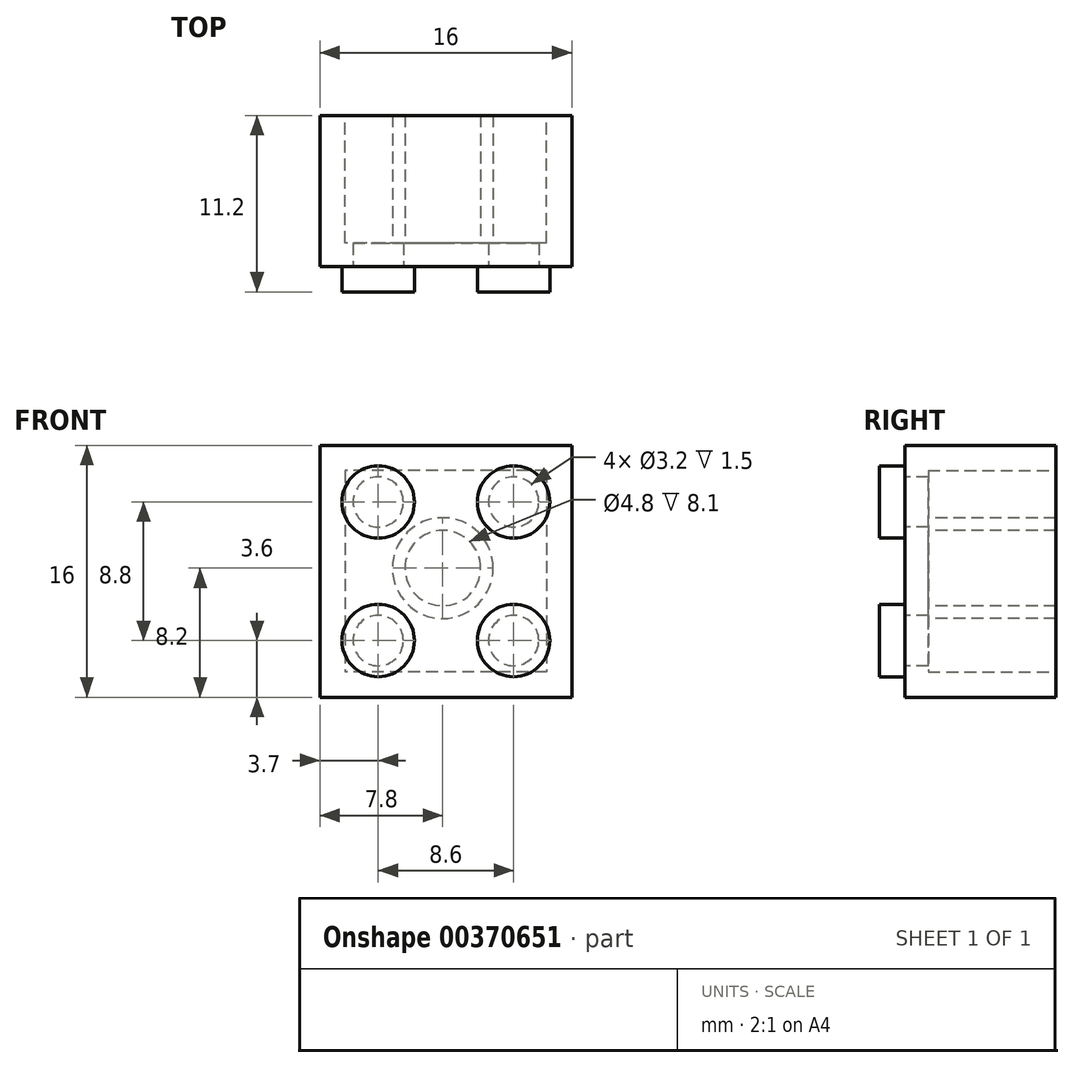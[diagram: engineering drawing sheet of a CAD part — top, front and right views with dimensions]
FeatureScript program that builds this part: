
annotation { "Feature Type Name" : "Feature", "Feature Type Description" : "" }
export const myFeature = defineFeature(function(context is Context, id is Id, definition is map)
    precondition{}
    {
        {
            var Q0;
            Q0=qCreatedBy(makeId("Front.planeOp"),FACE);
            var sketch = newSketch(context, id + "F0", { "sketchPlane" : qUnion([Q0])});
            skLineSegment(sketch, "E0.bottom", {"start": v(8, 8) * mm, "end": v(-8, 8) * mm});
            skLineSegment(sketch, "E0.top", {"start": v(8, -8) * mm, "end": v(-8, -8) * mm});
            skLineSegment(sketch, "E0.left", {"start": v(8, 8) * mm, "end": v(8, -8) * mm});
            skLineSegment(sketch, "E0.right", {"start": v(-8, 8) * mm, "end": v(-8, -8) * mm});
            skPoint(sketch, "E0.middle", {"position": v(0, 0) * mm});
            skLineSegment(sketch, "E1.0", {"start": v(6.4, 6.4) * mm, "end": v(-6.4, 6.4) * mm});
            skLineSegment(sketch, "E1.1", {"start": v(6.4, 6.4) * mm, "end": v(6.4, -6.4) * mm});
            skLineSegment(sketch, "E1.2", {"start": v(6.4, -6.4) * mm, "end": v(-6.4, -6.4) * mm});
            skLineSegment(sketch, "E1.3", {"start": v(-6.4, 6.4) * mm, "end": v(-6.4, -6.4) * mm});
            skSolve(sketch);
        }
        {
            var Q0;
            Q0 = qSketchRegion(id + "F0", true);
            var Q1;
            Q1=makeQuery(id+"F0.imprint","IMPRINT",FACE,{"disambiguationData":[TD([[makeQuery(id+"F0.imprint","IMPRINT",EDGE,{"derivedFrom":sQuery(id+"F0.wireOp",EDGE,"E1.0")}),1.0]])]});
            extrude(context, id + "F1", {"entities" : qUnion([Q0, Q1]), "depth" : 9.6 * mm});
        }
        {
            var Q0;
            Q0=makeQuery(id+"F0.imprint","IMPRINT",FACE,{"disambiguationData":[TD([[makeQuery(id+"F0.imprint","IMPRINT",EDGE,{"derivedFrom":sQuery(id+"F0.wireOp",EDGE,"E1.0")}),1.0]])]});
            extrude(context, id + "F2", {"entities" : qUnion([Q0]), "operationType" : NewBodyOperationType.REMOVE, "depth" : 8.1 * mm});
        }
        {
            var Q0;
            Q0=makeQuery(id+"F1.opExtrude","CAP_FACE",FACE,{"disambiguationData":[OSD([sQuery(id+"F0.wireOp",EDGE,"E0.bottom"),sQuery(id+"F0.wireOp",EDGE,"E0.top"),sQuery(id+"F0.wireOp",EDGE,"E0.left"),sQuery(id+"F0.wireOp",EDGE,"E0.right")])],"isStart":false});
            var sketch = newSketch(context, id + "F3", { "sketchPlane" : qUnion([Q0])});
            skCircle(sketch, "E2", {"center": v(-4.3, 4.4) * mm, "radius": 1.6 * mm});
            skCircle(sketch, "E3", {"center": v(-4.3, -4.4) * mm, "radius": 1.6 * mm});
            skCircle(sketch, "E4.MirrorC", {"center": v(4.3, 4.4) * mm, "radius": 1.6 * mm});
            skCircle(sketch, "E5.MirrorC", {"center": v(4.3, -4.4) * mm, "radius": 1.6 * mm});
            skSolve(sketch);
        }
        {
            var Q0;
            Q0 = qSketchRegion(id + "F3", true);
            extrude(context, id + "F4", {"entities" : qUnion([Q0]), "operationType" : NewBodyOperationType.REMOVE, "oppositeDirection" : true, "depth" : 1.6 * mm});
        }
        {
            var Q0;
            Q0=makeQuery(id+"F1.opExtrude","CAP_FACE",FACE,{"disambiguationData":[OSD([sQuery(id+"F0.wireOp",EDGE,"E0.bottom"),sQuery(id+"F0.wireOp",EDGE,"E0.top"),sQuery(id+"F0.wireOp",EDGE,"E0.left"),sQuery(id+"F0.wireOp",EDGE,"E0.right")])],"isStart":false});
            var sketch = newSketch(context, id + "F5", { "sketchPlane" : qUnion([Q0])});
            skCircle(sketch, "E6", {"center": v(-4.3, 4.4) * mm, "radius": 2.3 * mm});
            skCircle(sketch, "E7", {"center": v(-4.3, -4.4) * mm, "radius": 2.3 * mm});
            skCircle(sketch, "E8.MirrorC", {"center": v(4.3, 4.4) * mm, "radius": 2.3 * mm});
            skCircle(sketch, "E9.MirrorC", {"center": v(4.3, -4.4) * mm, "radius": 2.3 * mm});
            skSolve(sketch);
        }
        {
            var Q0;
            Q0 = qSketchRegion(id + "F5", true);
            extrude(context, id + "F6", {"entities" : qUnion([Q0]), "operationType" : NewBodyOperationType.ADD, "depth" : 1.6 * mm});
        }
        {
            var Q0;
            Q0=makeQuery(id+"F1.opExtrude","CAP_FACE",FACE,{"disambiguationData":[OSD([sQuery(id+"F0.wireOp",EDGE,"E0.bottom"),sQuery(id+"F0.wireOp",EDGE,"E0.top"),sQuery(id+"F0.wireOp",EDGE,"E0.left"),sQuery(id+"F0.wireOp",EDGE,"E0.right")])],"isStart":false});
            var sketch = newSketch(context, id + "F7", { "sketchPlane" : qUnion([Q0])});
            skCircle(sketch, "E10", {"center": v(-0.2, 0.2) * mm, "radius": 3.2 * mm});
            skCircle(sketch, "E11", {"center": v(-0.2, 0.2) * mm, "radius": 2.4 * mm});
            skSolve(sketch);
        }
        {
            var Q0;
            Q0 = qSketchRegion(id + "F7", true);
            extrude(context, id + "F8", {"entities" : qUnion([Q0]), "operationType" : NewBodyOperationType.ADD, "oppositeDirection" : true, "depth" : 9.6 * mm});
        }
    });
